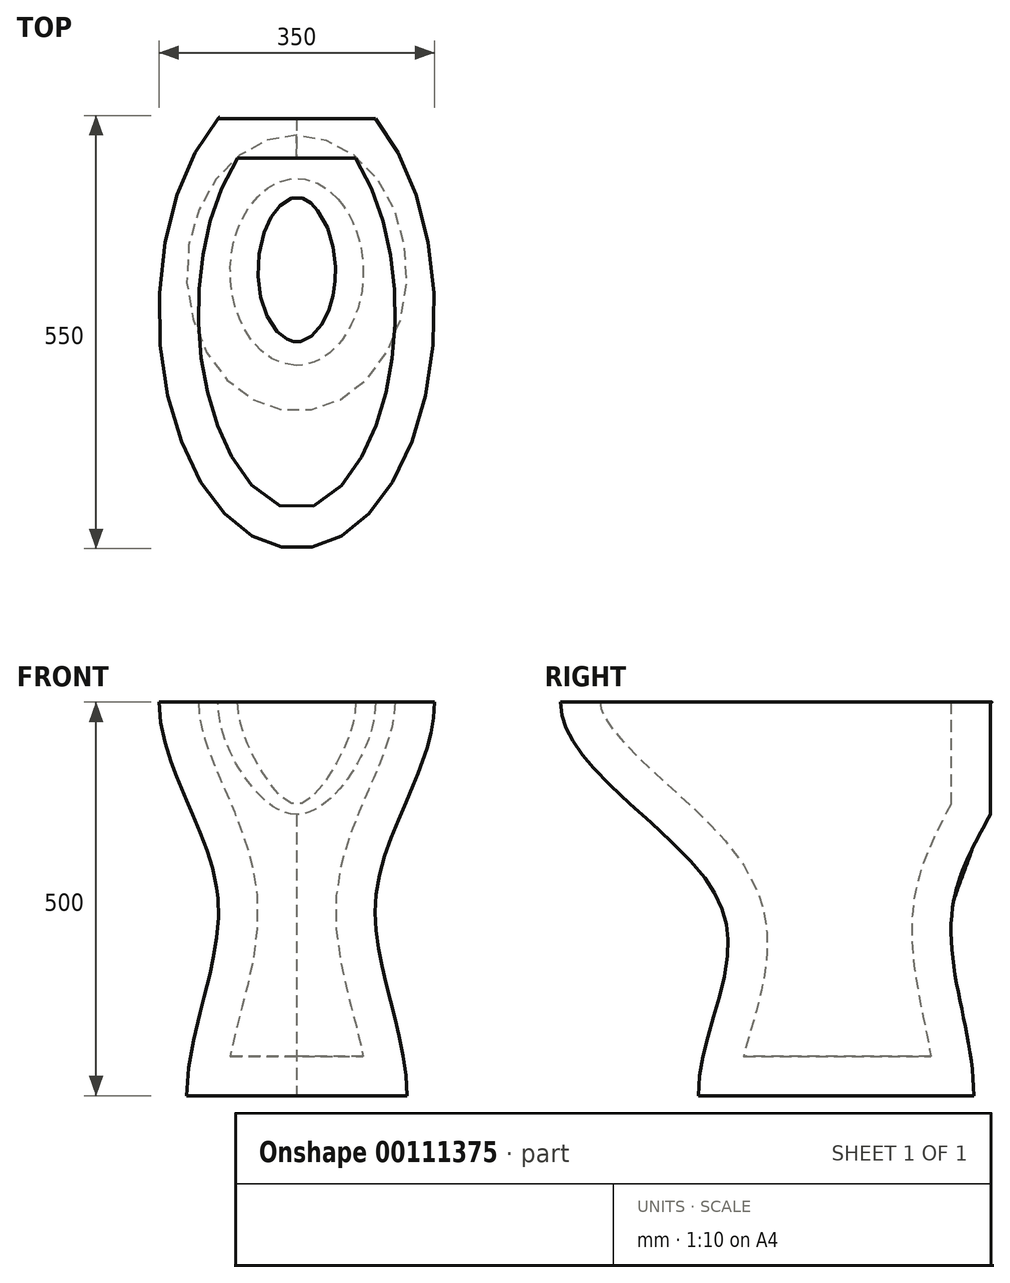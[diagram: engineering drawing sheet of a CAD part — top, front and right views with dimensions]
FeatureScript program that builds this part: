
annotation { "Feature Type Name" : "Feature", "Feature Type Description" : "" }
export const myFeature = defineFeature(function(context is Context, id is Id, definition is map)
    precondition{}
    {
        {
            var Q0;
            Q0=qCreatedBy(makeId("Top.planeOp"),FACE);
            cPlane(context, id + "F0", {"entities" : qUnion([Q0]), "cplaneType" : CPlaneType.OFFSET, "offset" : 250 * mm, "width" : 150 * mm, "height" : 150 * mm});
        }
        {
            var Q0;
            Q0=qCreatedBy(makeId("Top.planeOp"),FACE);
            cPlane(context, id + "F1", {"entities" : qUnion([Q0]), "cplaneType" : CPlaneType.OFFSET, "offset" : 500 * mm, "width" : 150 * mm, "height" : 150 * mm});
        }
        {
            var Q0;
            Q0=qCreatedBy(makeId("Top.planeOp"),FACE);
            var sketch = newSketch(context, id + "F2", { "sketchPlane" : qUnion([Q0])});
            skEllipse(sketch, "E0", {"center": v(0, 0) * mm, "majorRadius": 175 * mm, "minorRadius": 140 * mm, "majorAxis": v(0, 1)});
            skSolve(sketch);
        }
        {
            var Q0;
            Q0=qCreatedBy(id+"F0.planeOp",FACE);
            var sketch = newSketch(context, id + "F3", { "sketchPlane" : qUnion([Q0])});
            skEllipse(sketch, "E1", {"center": v(0, 0) * mm, "majorRadius": 150 * mm, "minorRadius": 100 * mm, "majorAxis": v(0, 1)});
            skSolve(sketch);
        }
        {
            var Q0;
            Q0=qCreatedBy(id+"F1.planeOp",FACE);
            var sketch = newSketch(context, id + "F4", { "sketchPlane" : qUnion([Q0])});
            skLineSegment(sketch, "E2", {"start": v(0, 0) * mm, "end": v(0, -50) * mm});
            skEllipse(sketch, "E3", {"center": v(0, -50) * mm, "majorRadius": 300 * mm, "minorRadius": 175 * mm, "majorAxis": v(0, 1)});
            skSolve(sketch);
        }
        {
            var Q0;
            Q0=makeQuery(id+"F4.imprint","IMPRINT",FACE,{"disambiguationData":[TD([[makeQuery(id+"F4.imprint","IMPRINT",EDGE,{"derivedFrom":sQuery(id+"F4.wireOp",EDGE,"E3")}),1.0]])]});
            var Q1;
            Q1=makeQuery(id+"F3.imprint","IMPRINT",FACE,{"disambiguationData":[TD([[makeQuery(id+"F3.imprint","IMPRINT",EDGE,{"derivedFrom":sQuery(id+"F3.wireOp",EDGE,"E1")}),1.0]])]});
            var Q2;
            Q2=makeQuery(id+"F2.imprint","IMPRINT",FACE,{"disambiguationData":[TD([[makeQuery(id+"F2.imprint","IMPRINT",EDGE,{"derivedFrom":sQuery(id+"F2.wireOp",EDGE,"E0")}),1.0]])]});
            loft(context, id + "F5", {"startCondition" : LoftEndDerivativeType.NORMAL_TO_PROFILE, "startMagnitude" : 1, "endCondition" : LoftEndDerivativeType.NORMAL_TO_PROFILE, "endMagnitude" : 1, "sheetProfilesArray" : [{ "sheetProfileEntities" : qUnion([Q0]) }, { "sheetProfileEntities" : qUnion([Q1]) }, { "sheetProfileEntities" : qUnion([Q2]) }]});
        }
        {
            var Q0;
            Q0=makeQuery(id+"F5.opLoft","CAP_FACE",FACE,{"disambiguationData":[OSD([makeQuery(id+"F4.imprint","IMPRINT",FACE,{"disambiguationData":[TD([[makeQuery(id+"F4.imprint","IMPRINT",EDGE,{"derivedFrom":sQuery(id+"F4.wireOp",EDGE,"E3")}),1.0]])]})])],"isStart":true});
            var sketch = newSketch(context, id + "F6", { "sketchPlane" : qUnion([Q0])});
            skLineSegment(sketch, "E4", {"start": v(-100, 196.2) * mm, "end": v(100, 196.2) * mm});
            skSolve(sketch);
        }
        {
            var Q0;
            {var subQ0=sQuery(id+"F6.wireOp",EDGE,"E4");Q0=makeQuery(id+"F6.imprint","IMPRINT",FACE,{"disambiguationData":[TD([[makeQuery(id+"F6.imprint","IMPRINT",EDGE,{"derivedFrom":subQ0}),1.0]])]});}
            extrude(context, id + "F7", {"entities" : qUnion([Q0]), "operationType" : NewBodyOperationType.REMOVE, "endBound" : BoundingType.THROUGH_ALL, "oppositeDirection" : true, "depth" : 25 * mm});
        }
        {
            var Q0;
            Q0=makeQuery(id+"F5.opLoft","CAP_FACE",FACE,{"disambiguationData":[OSD([makeQuery(id+"F4.imprint","IMPRINT",FACE,{"disambiguationData":[TD([[makeQuery(id+"F4.imprint","IMPRINT",EDGE,{"derivedFrom":sQuery(id+"F4.wireOp",EDGE,"E3")}),1.0]])]})])],"isStart":true});
            shell(context, id + "F8", {"entities" : qUnion([Q0]), "thickness" : 50 * mm});
        }
    });
